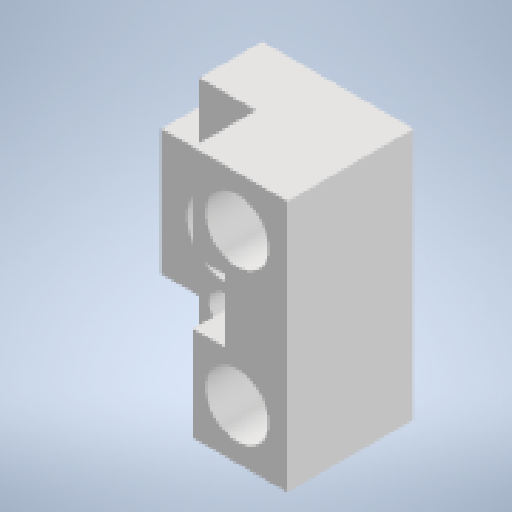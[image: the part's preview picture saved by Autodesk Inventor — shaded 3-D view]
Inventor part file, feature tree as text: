
AUTODESK INVENTOR PART (.ipt)
format: ipt  version: 2023 (Build 270158000, 158)  size: 233,984 bytes
history: native  units: mm
features: extrude x6, sketch x6
ambient origin geometry x8: Origin, YZ Plane, XZ Plane, XY Plane, X Axis, Y Axis, Z Axis, Center Point
bodies: Solid1 (feature_tree)
feature tree (12):
  extrude  "Extrusion1"  Depth=10.0mm
  extrude  "Extrusion2"  Depth=10.0mm
  extrude  "Extrusion6"  Depth=5.0mm
  extrude  "Extrusion7"  Depth=2.4mm
  extrude  "Extrusion8"  Depth=5.0mm TaperAngle=0.0deg
  extrude  "Extrusion9"  Depth=4.0mm
  sketch  "Sketch1"  dims[d0=10.0mm d1=10.0mm]
  sketch  "Sketch2"  dims[d2=10.0mm d3=10.0mm]
  sketch  "Sketch7"  dims[d4=5.0mm d5=5.0mm]
  sketch  "Sketch8"  dims[d6=2.4mm d7=2.4mm]
  sketch  "Sketch9"  dims[d8=6.0mm d9=5.0mm d10=0.0mm]
  sketch  "Sketch10"  dims[d17=1.0mm d18=0.0mm d34=4.0mm d35=4.0mm d36=4.0mm d37=4.0mm d38=5.0mm d39=5.0mm d40=2.75mm d41=2.75mm d42=5.0mm d43=0.0mm d44=7.5mm d45=7.5mm d46=7.5mm d47=7.5mm d48=5.0mm d49=5.0mm d50=0.0mm d51=4.0mm d52=4.0mm d53=2.0mm d54=0.0mm d55=5.0mm d56=3.0mm d57=5.0mm d58=5.0mm d59=3.0mm d60=10.0mm d61=0.0mm]
